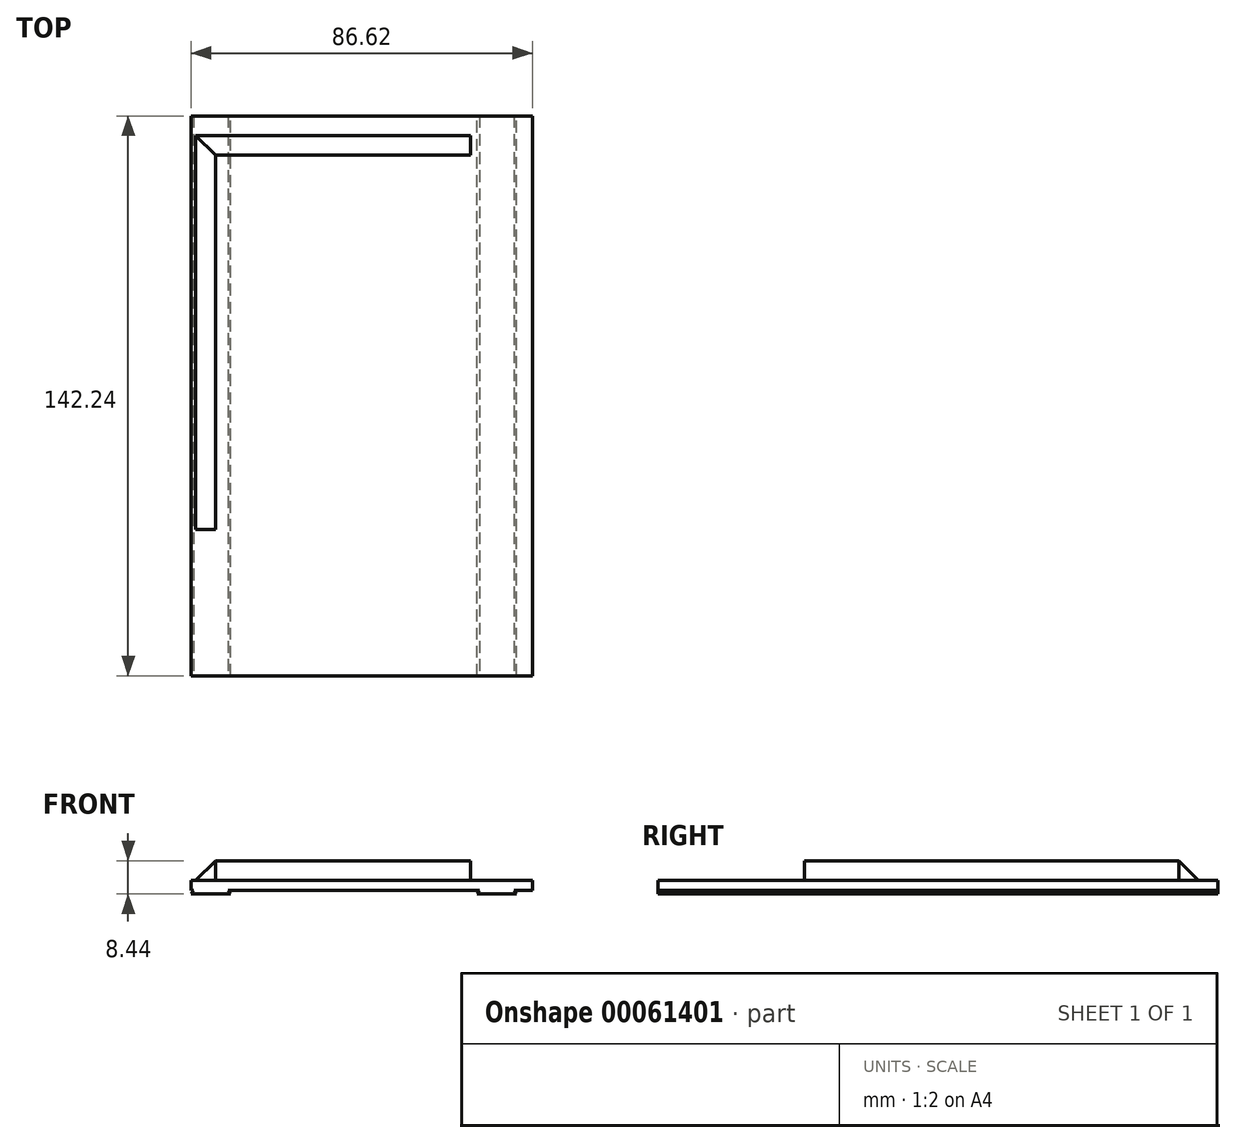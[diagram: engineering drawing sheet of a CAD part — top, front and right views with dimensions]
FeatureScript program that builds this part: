
annotation { "Feature Type Name" : "Feature", "Feature Type Description" : "" }
export const myFeature = defineFeature(function(context is Context, id is Id, definition is map)
    precondition{}
    {
        {
            var Q0;
            Q0=qCreatedBy(makeId("Front.planeOp"),FACE);
            var sketch = newSketch(context, id + "F0", { "sketchPlane" : qUnion([Q0])});
            skLineSegment(sketch, "E0.bottom", {"start": v(0, 0) * mm, "end": v(-96.52, 0) * mm});
            skLineSegment(sketch, "E0.top", {"start": v(0, 2.54) * mm, "end": v(-96.52, 2.54) * mm});
            skLineSegment(sketch, "E0.left", {"start": v(0, 0) * mm, "end": v(0, 2.54) * mm});
            skLineSegment(sketch, "E0.right", {"start": v(-96.52, 0) * mm, "end": v(-96.52, 2.54) * mm});
            skSolve(sketch);
        }
        {
            var Q0;
            Q0 = qSketchRegion(id + "F0", true);
            extrude(context, id + "F1", {"entities" : qUnion([Q0]), "depth" : 142.24 * mm});
        }
        {
            var Q0;
            Q0=makeQuery(id+"F1.opExtrude","SWEPT_FACE",FACE,{"disambiguationData":[OSD([sQuery(id+"F0.wireOp",EDGE,"E0.bottom")])]});
            var sketch = newSketch(context, id + "F2", { "sketchPlane" : qUnion([Q0])});
            skLineSegment(sketch, "E1.bottom", {"start": v(-86.61, 142.24) * mm, "end": v(-76.61, 142.24) * mm});
            skLineSegment(sketch, "E1.top", {"start": v(-86.61, 0) * mm, "end": v(-76.61, 0) * mm});
            skLineSegment(sketch, "E1.left", {"start": v(-86.61, 142.24) * mm, "end": v(-86.61, 0) * mm});
            skLineSegment(sketch, "E1.right", {"start": v(-76.61, 142.24) * mm, "end": v(-76.61, 0) * mm});
            skLineSegment(sketch, "E2.bottom", {"start": v(-14.01, 142.24) * mm, "end": v(-4.01, 142.24) * mm});
            skLineSegment(sketch, "E2.top", {"start": v(-14.01, 0) * mm, "end": v(-4.01, 0) * mm});
            skLineSegment(sketch, "E2.left", {"start": v(-14.01, 142.24) * mm, "end": v(-14.01, 0) * mm});
            skLineSegment(sketch, "E2.right", {"start": v(-4.01, 142.24) * mm, "end": v(-4.01, 0) * mm});
            skSolve(sketch);
        }
        {
            var Q0;
            Q0 = qSketchRegion(id + "F2", true);
            extrude(context, id + "F3", {"entities" : qUnion([Q0]), "operationType" : NewBodyOperationType.ADD, "depth" : 0.9 * mm});
        }
        {
            var Q0;
            Q0=makeQuery(id+"F3.boolean.opBoolean","MERGE",FACE,{"derivedFrom":[makeQuery(id+"F1.opExtrude","CAP_FACE",FACE,{"disambiguationData":[OSD([sQuery(id+"F0.wireOp",EDGE,"E0.bottom"),sQuery(id+"F0.wireOp",EDGE,"E0.top"),sQuery(id+"F0.wireOp",EDGE,"E0.left"),sQuery(id+"F0.wireOp",EDGE,"E0.right")])],"isStart":false}),makeQuery(id+"F3.opExtrude","SWEPT_FACE",FACE,{"disambiguationData":[OSD([sQuery(id+"F2.wireOp",EDGE,"E1.bottom")])]}),makeQuery(id+"F3.opExtrude","SWEPT_FACE",FACE,{"disambiguationData":[OSD([sQuery(id+"F2.wireOp",EDGE,"E2.bottom")])]})]});
            var sketch = newSketch(context, id + "F4", { "sketchPlane" : qUnion([Q0])});
            skLineSegment(sketch, "E3", {"start": v(-86.61, -0.9) * mm, "end": v(-86, 0) * mm});
            skLineSegment(sketch, "E4", {"start": v(-86, 0) * mm, "end": v(-86.61, 0) * mm});
            skLineSegment(sketch, "E5", {"start": v(-86.61, 0) * mm, "end": v(-86.61, -0.9) * mm});
            skLineSegment(sketch, "E6", {"start": v(-76.61, -0.9) * mm, "end": v(-77.22, 0) * mm});
            skLineSegment(sketch, "E7", {"start": v(-77.22, 0) * mm, "end": v(-76.61, 0) * mm});
            skLineSegment(sketch, "E8", {"start": v(-76.61, 0) * mm, "end": v(-76.61, -0.9) * mm});
            skLineSegment(sketch, "E9", {"start": v(-14.01, -0.9) * mm, "end": v(-13.4, 0) * mm});
            skLineSegment(sketch, "E10", {"start": v(-13.4, 0) * mm, "end": v(-14.01, 0) * mm});
            skLineSegment(sketch, "E11", {"start": v(-14.01, 0) * mm, "end": v(-14.01, -0.9) * mm});
            skLineSegment(sketch, "E12", {"start": v(-4.01, -0.9) * mm, "end": v(-4.62, 0) * mm});
            skLineSegment(sketch, "E13", {"start": v(-4.62, 0) * mm, "end": v(-4.01, 0) * mm});
            skLineSegment(sketch, "E14", {"start": v(-4.01, 0) * mm, "end": v(-4.01, -0.9) * mm});
            skSolve(sketch);
        }
        {
            var Q0;
            Q0 = qSketchRegion(id + "F4", true);
            extrude(context, id + "F5", {"entities" : qUnion([Q0]), "operationType" : NewBodyOperationType.REMOVE, "endBound" : BoundingType.THROUGH_ALL, "oppositeDirection" : true, "depth" : 25 * mm});
        }
        {
            var Q0;
            Q0=makeQuery(id+"F1.opExtrude","SWEPT_FACE",FACE,{"disambiguationData":[OSD([sQuery(id+"F0.wireOp",EDGE,"E0.top")])]});
            var sketch = newSketch(context, id + "F6", { "sketchPlane" : qUnion([Q0])});
            skLineSegment(sketch, "E15.bottom", {"start": v(-91.52, -5) * mm, "end": v(-21.52, -5) * mm});
            skLineSegment(sketch, "E15.top", {"start": v(-91.52, -105) * mm, "end": v(-21.52, -105) * mm});
            skLineSegment(sketch, "E15.left", {"start": v(-91.52, -5) * mm, "end": v(-91.52, -105) * mm});
            skLineSegment(sketch, "E15.right", {"start": v(-21.52, -5) * mm, "end": v(-21.52, -105) * mm});
            skSolve(sketch);
        }
        {
            var Q0;
            Q0=makeQuery(id+"F6.imprint","IMPRINT",FACE,{"disambiguationData":[TD([[makeQuery(id+"F6.imprint","IMPRINT",EDGE,{"derivedFrom":sQuery(id+"F6.wireOp",EDGE,"E15.bottom")}),1.0]])]});
            var sketch = newSketch(context, id + "F7", { "sketchPlane" : qUnion([Q0])});
            skLineSegment(sketch, "E16.top", {"start": v(-85.52, -5) * mm, "end": v(-15.67, -5) * mm});
            skLineSegment(sketch, "E16.right", {"start": v(-15.67, -10) * mm, "end": v(-15.67, -5) * mm});
            skLineSegment(sketch, "E17.top", {"start": v(-85.52, -105.08) * mm, "end": v(-80.52, -105.08) * mm});
            skLineSegment(sketch, "E17.left", {"start": v(-85.52, -5) * mm, "end": v(-85.52, -105.08) * mm});
            skLineSegment(sketch, "E18", {"start": v(-15.67, -10) * mm, "end": v(-80.52, -10) * mm});
            skLineSegment(sketch, "E19", {"start": v(-80.52, -10) * mm, "end": v(-80.52, -105.08) * mm});
            skSolve(sketch);
        }
        {
            var Q0;
            Q0 = qSketchRegion(id + "F7", true);
            extrude(context, id + "F8", {"entities" : qUnion([Q0]), "operationType" : NewBodyOperationType.ADD, "depth" : 5 * mm});
        }
        {
            var Q0;
            Q0=makeQuery(id+"F8.opExtrude","CAP_EDGE",EDGE,{"disambiguationData":[OSD([sQuery(id+"F7.wireOp",EDGE,"E17.left")])],"isStart":false});
            var Q1;
            Q1=makeQuery(id+"F8.opExtrude","CAP_EDGE",EDGE,{"disambiguationData":[OSD([sQuery(id+"F7.wireOp",EDGE,"E16.top")])],"isStart":false});
            chamfer(context, id + "F9", {"entities" : qUnion([Q0, Q1]), "width" : 5 * mm, "tangentPropagation" : true});
        }
        {
            var Q0;
            Q0=makeQuery(id+"F6.imprint","IMPRINT",FACE,{"disambiguationData":[TD([[makeQuery(id+"F6.imprint","IMPRINT",EDGE,{"derivedFrom":sQuery(id+"F6.wireOp",EDGE,"E15.bottom")}),1.0]])]});
            var sketch = newSketch(context, id + "F10", { "sketchPlane" : qUnion([Q0])});
            skLineSegment(sketch, "E20.bottom", {"start": v(-96.52, 0) * mm, "end": v(-86.62, 0) * mm});
            skLineSegment(sketch, "E20.top", {"start": v(-96.52, -142.24) * mm, "end": v(-86.62, -142.24) * mm});
            skLineSegment(sketch, "E20.left", {"start": v(-96.52, 0) * mm, "end": v(-96.52, -142.24) * mm});
            skLineSegment(sketch, "E20.right", {"start": v(-86.62, 0) * mm, "end": v(-86.62, -142.24) * mm});
            skSolve(sketch);
        }
        {
            var Q0;
            Q0 = qSketchRegion(id + "F10", true);
            extrude(context, id + "F11", {"entities" : qUnion([Q0]), "operationType" : NewBodyOperationType.REMOVE, "endBound" : BoundingType.THROUGH_ALL, "oppositeDirection" : true, "depth" : 25 * mm});
        }
    });
